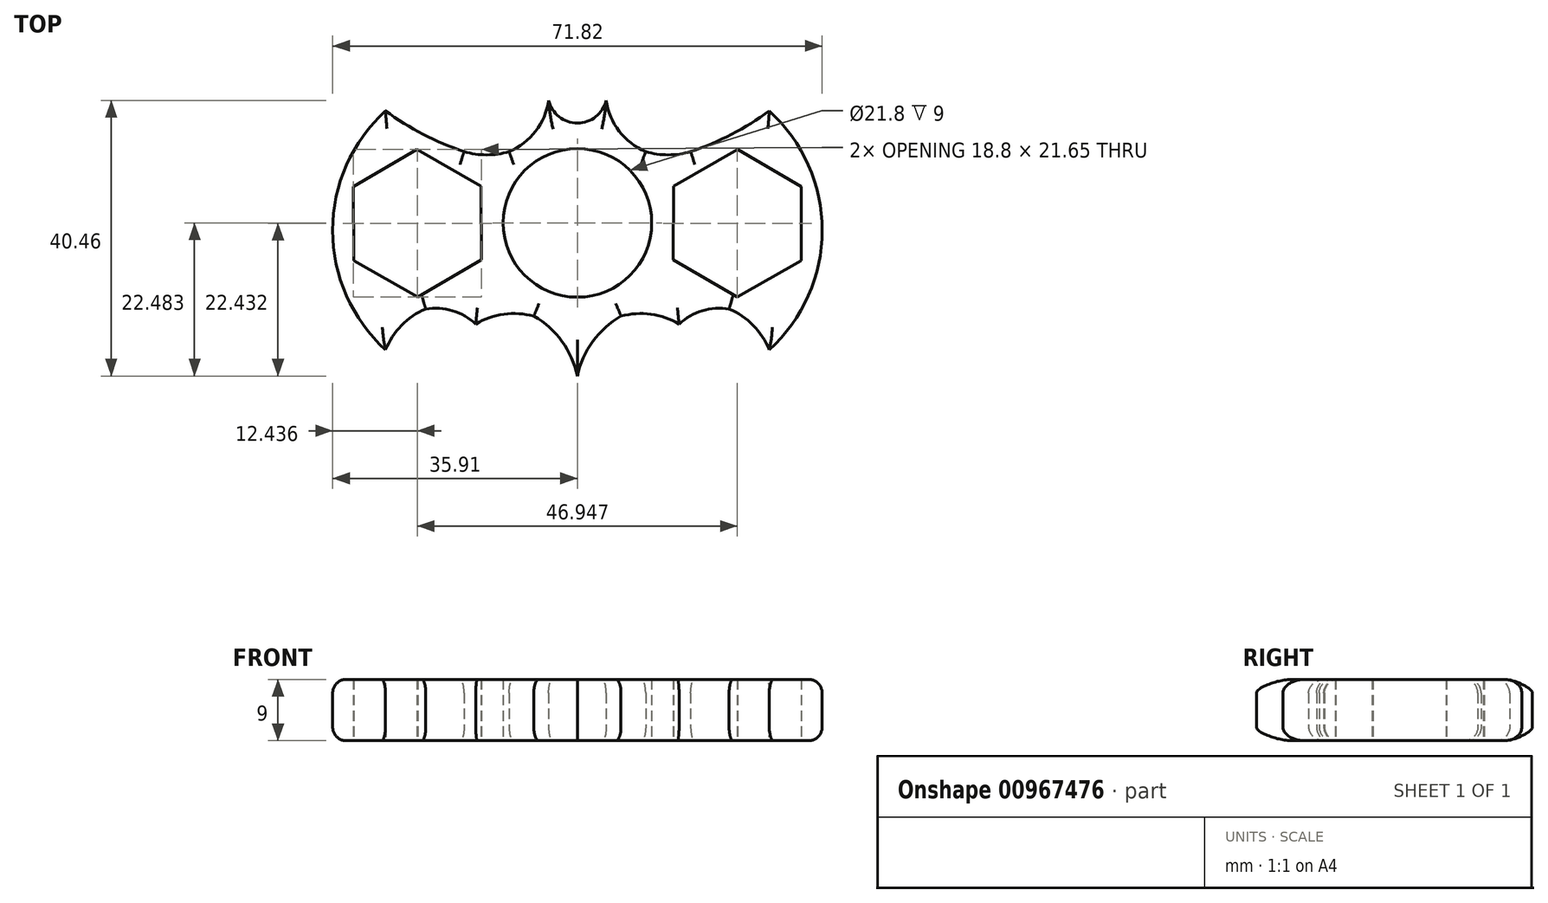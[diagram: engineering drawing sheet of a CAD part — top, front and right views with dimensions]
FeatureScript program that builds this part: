
annotation { "Feature Type Name" : "Feature", "Feature Type Description" : "" }
export const myFeature = defineFeature(function(context is Context, id is Id, definition is map)
    precondition{}
    {
        {
            var Q0;
            Q0=qCreatedBy(makeId("Top.planeOp"),FACE);
            var sketch = newSketch(context, id + "F0", { "sketchPlane" : qUnion([Q0])});
            skArc(sketch, "E0", {"start": v(-10.02, 12.8) * mm, "mid": v(-6.12, 15.78) * mm, "end": v(-4.22, 20.3) * mm});
            skPoint(sketch, "E1", {"position": v(0, 16.17) * mm});
            skArc(sketch, "E2", {"start": v(-16.62, 12.8) * mm, "mid": v(-13.32, 12.3) * mm, "end": v(-10.02, 12.8) * mm});
            skArc(sketch, "E3", {"start": v(-28.15, 18.76) * mm, "mid": v(-22.62, 15.32) * mm, "end": v(-16.62, 12.8) * mm});
            skArc(sketch, "E4", {"start": v(-28.15, 18.76) * mm, "mid": v(-35.9, 1.23) * mm, "end": v(-28.15, -16.3) * mm});
            skArc(sketch, "E5", {"start": v(-22.26, -10.3) * mm, "mid": v(-25.8, -12.72) * mm, "end": v(-28.15, -16.3) * mm});
            skArc(sketch, "E6", {"start": v(-14.91, -12.53) * mm, "mid": v(-18.33, -10.56) * mm, "end": v(-22.26, -10.3) * mm});
            skArc(sketch, "E7", {"start": v(-6.4, -11.36) * mm, "mid": v(-10.78, -11.07) * mm, "end": v(-14.91, -12.53) * mm});
            skArc(sketch, "E8", {"start": v(0, -20.16) * mm, "mid": v(-2.25, -15.07) * mm, "end": v(-6.4, -11.36) * mm});
            skArc(sketch, "E9.MirrorCS", {"start": v(10.02, 12.8) * mm, "mid": v(6.12, 15.78) * mm, "end": v(4.22, 20.3) * mm});
            skArc(sketch, "E10.MirrorCS", {"start": v(16.62, 12.8) * mm, "mid": v(13.32, 12.3) * mm, "end": v(10.02, 12.8) * mm});
            skArc(sketch, "E11.MirrorCS", {"start": v(28.15, 18.76) * mm, "mid": v(22.62, 15.32) * mm, "end": v(16.62, 12.8) * mm});
            skArc(sketch, "E12.MirrorCS", {"start": v(28.15, 18.76) * mm, "mid": v(35.9, 1.23) * mm, "end": v(28.15, -16.3) * mm});
            skArc(sketch, "E13.MirrorCS", {"start": v(22.26, -10.3) * mm, "mid": v(25.8, -12.72) * mm, "end": v(28.15, -16.3) * mm});
            skArc(sketch, "E14.MirrorCS", {"start": v(14.91, -12.53) * mm, "mid": v(18.33, -10.56) * mm, "end": v(22.26, -10.3) * mm});
            skArc(sketch, "E15.MirrorCS", {"start": v(6.4, -11.36) * mm, "mid": v(10.78, -11.07) * mm, "end": v(14.91, -12.53) * mm});
            skArc(sketch, "E16.MirrorCS", {"start": v(0, -20.16) * mm, "mid": v(2.25, -15.07) * mm, "end": v(6.4, -11.36) * mm});
            skArc(sketch, "E17", {"start": v(-4.22, 20.3) * mm, "mid": v(0, 16.97) * mm, "end": v(4.22, 20.3) * mm});
            skSolve(sketch);
        }
        {
            var Q0;
            Q0=makeQuery(id+"F0.imprint","IMPRINT",FACE,{"disambiguationData":[TD([[makeQuery(id+"F0.imprint","IMPRINT",EDGE,{"derivedFrom":sQuery(id+"F0.wireOp",EDGE,"E0")}),-1.0]])]});
            extrude(context, id + "F1", {"entities" : qUnion([Q0]), "depth" : 9 * mm, "offsetDistance" : 25 * mm});
        }
        {
            var Q0;
            Q0=makeQuery(id+"F1.opExtrude","CAP_FACE",FACE,{"disambiguationData":[OSD([sQuery(id+"F0.wireOp",EDGE,"E0"),sQuery(id+"F0.wireOp",EDGE,"E2"),sQuery(id+"F0.wireOp",EDGE,"E3"),sQuery(id+"F0.wireOp",EDGE,"E4"),sQuery(id+"F0.wireOp",EDGE,"E5"),sQuery(id+"F0.wireOp",EDGE,"E6"),sQuery(id+"F0.wireOp",EDGE,"E7"),sQuery(id+"F0.wireOp",EDGE,"E8"),sQuery(id+"F0.wireOp",EDGE,"E9.MirrorCS"),sQuery(id+"F0.wireOp",EDGE,"E10.MirrorCS"),sQuery(id+"F0.wireOp",EDGE,"E11.MirrorCS"),sQuery(id+"F0.wireOp",EDGE,"E12.MirrorCS"),sQuery(id+"F0.wireOp",EDGE,"E13.MirrorCS"),sQuery(id+"F0.wireOp",EDGE,"E14.MirrorCS"),sQuery(id+"F0.wireOp",EDGE,"E15.MirrorCS"),sQuery(id+"F0.wireOp",EDGE,"E16.MirrorCS"),sQuery(id+"F0.wireOp",EDGE,"E17")])],"isStart":false});
            var Q1;
            Q1=makeQuery(id+"F1.opExtrude","CAP_FACE",FACE,{"disambiguationData":[OSD([sQuery(id+"F0.wireOp",EDGE,"E0"),sQuery(id+"F0.wireOp",EDGE,"E2"),sQuery(id+"F0.wireOp",EDGE,"E3"),sQuery(id+"F0.wireOp",EDGE,"E4"),sQuery(id+"F0.wireOp",EDGE,"E5"),sQuery(id+"F0.wireOp",EDGE,"E6"),sQuery(id+"F0.wireOp",EDGE,"E7"),sQuery(id+"F0.wireOp",EDGE,"E8"),sQuery(id+"F0.wireOp",EDGE,"E9.MirrorCS"),sQuery(id+"F0.wireOp",EDGE,"E10.MirrorCS"),sQuery(id+"F0.wireOp",EDGE,"E11.MirrorCS"),sQuery(id+"F0.wireOp",EDGE,"E12.MirrorCS"),sQuery(id+"F0.wireOp",EDGE,"E13.MirrorCS"),sQuery(id+"F0.wireOp",EDGE,"E14.MirrorCS"),sQuery(id+"F0.wireOp",EDGE,"E15.MirrorCS"),sQuery(id+"F0.wireOp",EDGE,"E16.MirrorCS"),sQuery(id+"F0.wireOp",EDGE,"E17")])],"isStart":true});
            fillet(context, id + "F2", {"entities" : qUnion([Q0, Q1]), "radius" : 2 * mm, "tangentPropagation" : true, "allowEdgeOverflow" : false});
        }
        {
            var Q0;
            Q0=qCreatedBy(makeId("Top.planeOp"),FACE);
            var sketch = newSketch(context, id + "F3", { "sketchPlane" : qUnion([Q0])});
            skLineSegment(sketch, "E18", {"start": v(-11.7, 2.32) * mm, "end": v(11.67, 2.32) * mm, "construction": true});
            skCircle(sketch, "E19", {"center": v(0, 2.32) * mm, "radius": 10.9 * mm});
            skSolve(sketch);
        }
        {
            var Q0;
            Q0 = qSketchRegion(id + "F3", true);
            extrude(context, id + "F4", {"entities" : qUnion([Q0]), "operationType" : NewBodyOperationType.REMOVE, "depth" : 25 * mm, "offsetDistance" : 25 * mm});
        }
        {
            var Q0;
            Q0=qCreatedBy(makeId("Top.planeOp"),FACE);
            var sketch = newSketch(context, id + "F5", { "sketchPlane" : qUnion([Q0])});
            skCircle(sketch, "E20.cCircle", {"center": v(-23.47, 2.27) * mm, "radius": 9.38 * mm, "construction": true});
            skLineSegment(sketch, "E20.0", {"start": v(-14.07, -3.1) * mm, "end": v(-23.42, -8.55) * mm});
            skLineSegment(sketch, "E20.1", {"start": v(-23.42, -8.55) * mm, "end": v(-32.82, -3.18) * mm});
            skLineSegment(sketch, "E20.2", {"start": v(-32.82, -3.18) * mm, "end": v(-32.87, 7.64) * mm});
            skLineSegment(sketch, "E20.3", {"start": v(-32.87, 7.64) * mm, "end": v(-23.52, 13.1) * mm});
            skLineSegment(sketch, "E20.4", {"start": v(-23.52, 13.1) * mm, "end": v(-14.12, 7.73) * mm});
            skLineSegment(sketch, "E20.5", {"start": v(-14.12, 7.73) * mm, "end": v(-14.07, -3.1) * mm});
            skPoint(sketch, "E20.0.midPoint", {"position": v(-18.75, -5.83) * mm});
            skLineSegment(sketch, "E21.MirrorCS", {"start": v(32.87, 7.64) * mm, "end": v(23.52, 13.1) * mm});
            skLineSegment(sketch, "E22.MirrorCS", {"start": v(32.82, -3.18) * mm, "end": v(32.87, 7.64) * mm});
            skLineSegment(sketch, "E23.MirrorCS", {"start": v(23.42, -8.55) * mm, "end": v(32.82, -3.18) * mm});
            skLineSegment(sketch, "E24.MirrorCS", {"start": v(14.07, -3.1) * mm, "end": v(23.42, -8.55) * mm});
            skLineSegment(sketch, "E25.MirrorCS", {"start": v(14.12, 7.73) * mm, "end": v(14.07, -3.1) * mm});
            skLineSegment(sketch, "E26.MirrorCS", {"start": v(23.52, 13.1) * mm, "end": v(14.12, 7.73) * mm});
            skSolve(sketch);
        }
        {
            var Q0;
            Q0 = qSketchRegion(id + "F5", true);
            extrude(context, id + "F6", {"entities" : qUnion([Q0]), "operationType" : NewBodyOperationType.REMOVE, "depth" : 25 * mm, "offsetDistance" : 25 * mm});
        }
    });
